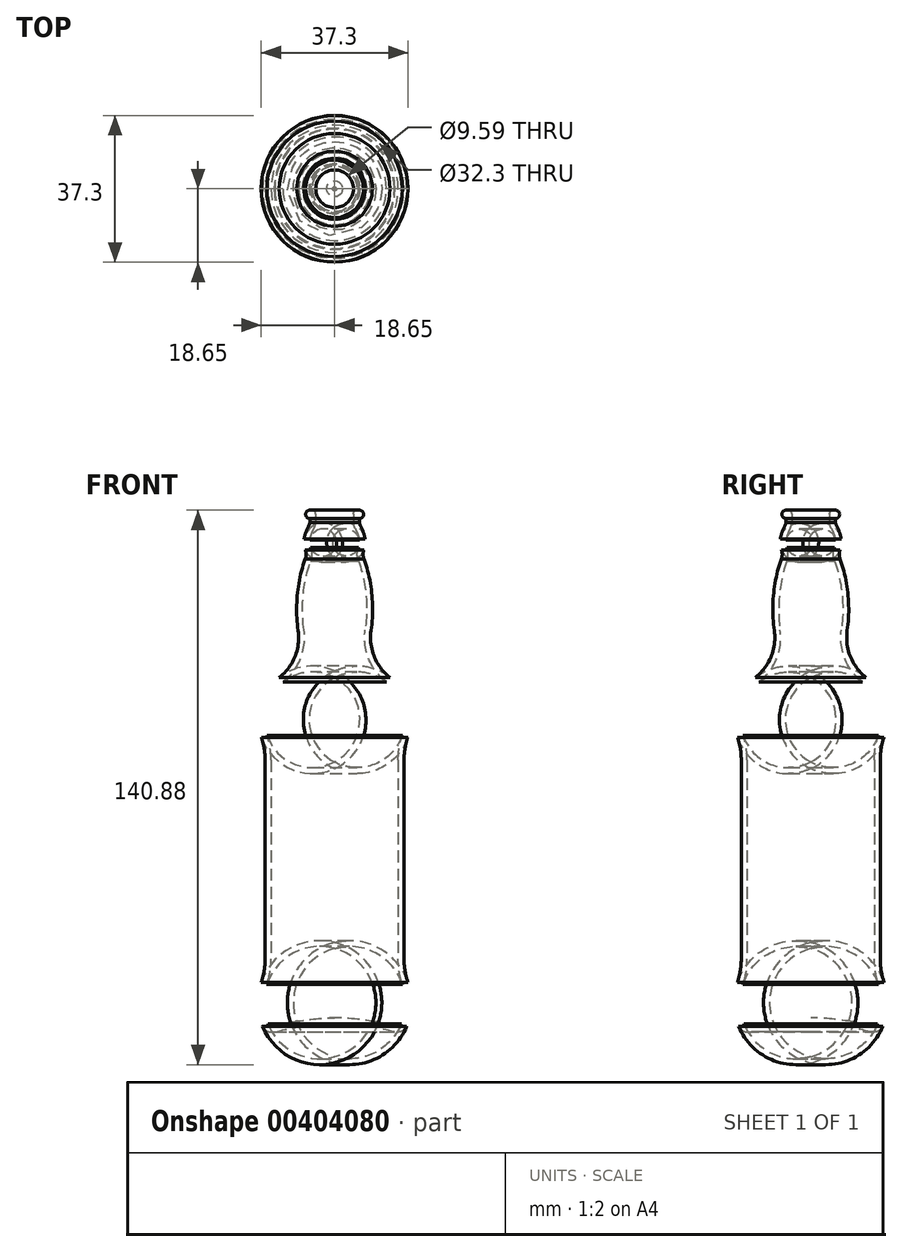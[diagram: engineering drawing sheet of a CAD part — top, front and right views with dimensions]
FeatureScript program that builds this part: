
annotation { "Feature Type Name" : "Feature", "Feature Type Description" : "" }
export const myFeature = defineFeature(function(context is Context, id is Id, definition is map)
    precondition{}
    {
        {
            var Q0;
            Q0=qCreatedBy(makeId("Front.planeOp"),FACE);
            var sketch = newSketch(context, id + "F0", { "sketchPlane" : qUnion([Q0])});
            skLineSegment(sketch, "E0.bottom", {"start": v(15.17, 0) * mm, "end": v(16.2, 0) * mm});
            skLineSegment(sketch, "E0.left", {"start": v(0, 2.09) * mm, "end": v(0, 81.73) * mm});
            skLineSegment(sketch, "E0.right", {"start": v(17.65, 18.52) * mm, "end": v(17.65, 69.06) * mm});
            skLineSegment(sketch, "E1.top", {"start": v(0, 132.57) * mm, "end": v(6.3, 132.57) * mm});
            skLineSegment(sketch, "E1.left", {"start": v(0, 81.73) * mm, "end": v(0, 132.57) * mm});
            skLineSegment(sketch, "E1.right", {"start": v(6.3, 129.42) * mm, "end": v(6.3, 130.45) * mm});
            skArc(sketch, "E2", {"start": v(6.3, 130.45) * mm, "mid": v(7.35, 131.51) * mm, "end": v(6.3, 132.57) * mm});
            skPoint(sketch, "E2.second.point", {"position": v(6.3, 130.45) * mm});
            skPoint(sketch, "E2.third.point", {"position": v(6.3, 132.57) * mm});
            skArc(sketch, "E3", {"start": v(18.33, 1.43) * mm, "mid": v(19.51, 7) * mm, "end": v(18.65, 12.61) * mm});
            skArc(sketch, "E4", {"start": v(18.62, 74.88) * mm, "mid": v(18.78, 83.22) * mm, "end": v(14.07, 90.1) * mm});
            skArc(sketch, "E5", {"start": v(9.25, 101.97) * mm, "mid": v(10.06, 95.38) * mm, "end": v(14.07, 90.1) * mm});
            skArc(sketch, "E6", {"start": v(9.25, 101.97) * mm, "mid": v(9.46, 111.2) * mm, "end": v(7.47, 120.22) * mm});
            skArc(sketch, "E7", {"start": v(7.47, 122.51) * mm, "mid": v(7.24, 121.37) * mm, "end": v(7.47, 120.22) * mm});
            skArc(sketch, "E8", {"start": v(7.47, 122.51) * mm, "mid": v(7.8, 123.87) * mm, "end": v(7.75, 125.27) * mm});
            skArc(sketch, "E9", {"start": v(7.75, 125.27) * mm, "mid": v(7.3, 126.97) * mm, "end": v(6.59, 128.58) * mm});
            skArc(sketch, "E10", {"start": v(6.3, 129.42) * mm, "mid": v(6.4, 128.99) * mm, "end": v(6.59, 128.58) * mm});
            skPoint(sketch, "E11.visualSharp", {"position": v(17.65, 0) * mm});
            skArc(sketch, "E11.filletArc", {"start": v(16.2, 0) * mm, "mid": v(17.48, 0.39) * mm, "end": v(18.33, 1.43) * mm});
            skPoint(sketch, "E12.visualSharp", {"position": v(17.65, 14.89) * mm});
            skArc(sketch, "E12.filletArc", {"start": v(17.65, 18.52) * mm, "mid": v(17.9, 15.52) * mm, "end": v(18.65, 12.61) * mm});
            skPoint(sketch, "E13.visualSharp", {"position": v(17.65, 72.7) * mm});
            skArc(sketch, "E13.filletArc", {"start": v(18.62, 74.88) * mm, "mid": v(17.9, 72.01) * mm, "end": v(17.65, 69.06) * mm});
            skArc(sketch, "E14", {"start": v(15.17, 0) * mm, "mid": v(7.65, 1.51) * mm, "end": v(0, 2.09) * mm});
            skSolve(sketch);
        }
        {
            var Q0;
            Q0=makeQuery(id+"F0.imprint","IMPRINT",FACE,{"disambiguationData":[TD([[makeQuery(id+"F0.imprint","IMPRINT",EDGE,{"derivedFrom":sQuery(id+"F0.wireOp",EDGE,"E0.bottom")}),1.0]])]});
            var Q1;
            Q1=sQuery(id+"F0.wireOp",EDGE,"E0.left");
            revolve(context, id + "F1", {"surfaceOperationType" : NewSurfaceOperationType.NEW, "entities" : qUnion([Q0]), "axis" : qUnion([Q1]), "revolveType" : RevolveType.FULL});
        }
        {
            var Q0;
            Q0=makeQuery(id+"F1.opRevolve","SWEPT_FACE",FACE,{"disambiguationData":[OSD([sQuery(id+"F0.wireOp",EDGE,"E1.top")])]});
            shell(context, id + "F2", {"entities" : qUnion([Q0]), "thickness" : 1.5 * mm});
        }
        {
            var Q0;
            Q0=makeQuery(id+"F2.opShell","OFFSET_EDGE",EDGE,{"disambiguationData":[OSD([sQuery(id+"F0.wireOp",EDGE,"E1.top"),sQuery(id+"F0.wireOp",EDGE,"E1.right"),sQuery(id+"F0.wireOp",EDGE,"E2")])]});
            fillet(context, id + "F3", {"entities" : qUnion([Q0]), "tangentPropagation" : true, "radius" : 1 * mm, "defaultsChanged" : true, "vertexSettings" : [], "allowEdgeOverflow" : false});
        }
    });
